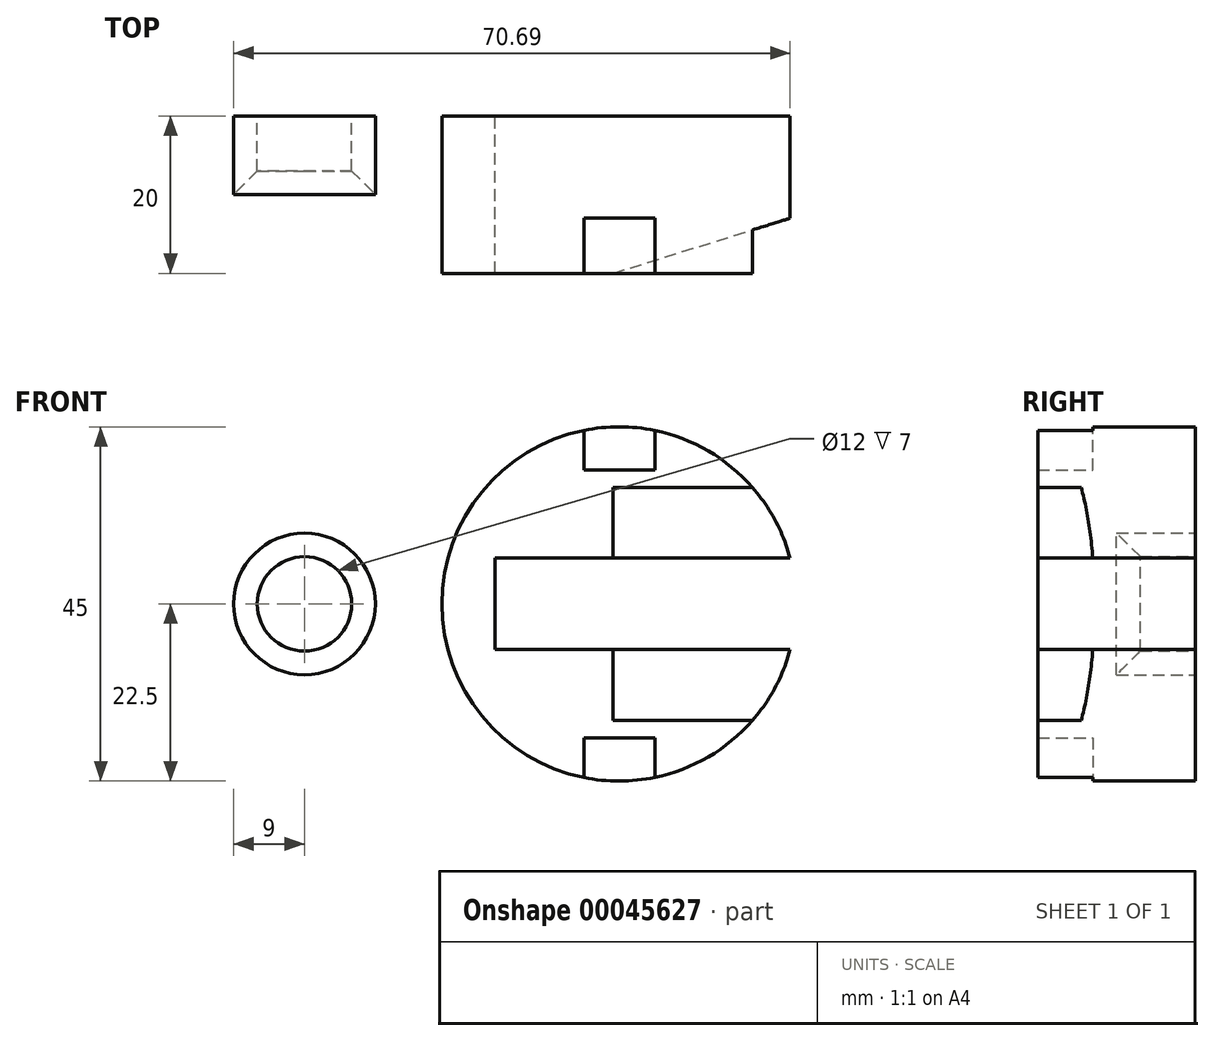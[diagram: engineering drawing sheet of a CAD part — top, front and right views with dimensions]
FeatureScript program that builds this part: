
annotation { "Feature Type Name" : "Feature", "Feature Type Description" : "" }
export const myFeature = defineFeature(function(context is Context, id is Id, definition is map)
    precondition{}
    {
        {
            var Q0;
            Q0=qCreatedBy(makeId("Front.planeOp"),FACE);
            var sketch = newSketch(context, id + "F0", { "sketchPlane" : qUnion([Q0])});
            skArc(sketch, "E0", {"start": v(-24.5, 0) * mm, "mid": v(-20.99, -8.49) * mm, "end": v(-12.5, -12) * mm});
            skLineSegment(sketch, "E1", {"start": v(-24.5, 0) * mm, "end": v(79.5, 0) * mm, "construction": true});
            skArc(sketch, "E2", {"start": v(-18.5, 0) * mm, "mid": v(-12.5, -6) * mm, "end": v(-6.5, 0) * mm});
            skArc(sketch, "E3", {"start": v(-21.5, 0) * mm, "mid": v(-12.5, -9) * mm, "end": v(-3.5, 0) * mm});
            skArc(sketch, "E4", {"start": v(4.95, 0) * mm, "mid": v(24.52, -22.3) * mm, "end": v(49.19, -5.8) * mm});
            skLineSegment(sketch, "E5", {"start": v(-12.5, -12) * mm, "end": v(6.27, -12) * mm});
            skArc(sketch, "E6", {"start": v(6.27, -12) * mm, "mid": v(7.65, -12.2) * mm, "end": v(8.92, -12.76) * mm});
            skLineSegment(sketch, "E7", {"start": v(11.69, -5.8) * mm, "end": v(49.19, -5.8) * mm});
            skLineSegment(sketch, "E8", {"start": v(11.69, -5.8) * mm, "end": v(11.69, 0) * mm});
            skLineSegment(sketch, "E9", {"start": v(27.5, -17) * mm, "end": v(32, -17) * mm});
            skLineSegment(sketch, "E10", {"start": v(23, -17) * mm, "end": v(23, -22.06) * mm});
            skLineSegment(sketch, "E11", {"start": v(32, -17) * mm, "end": v(32, -22.04) * mm});
            skLineSegment(sketch, "E12", {"start": v(27.5, -17) * mm, "end": v(23, -17) * mm});
            skArc(sketch, "E13.MirrorCS", {"start": v(-18.5, 0) * mm, "mid": v(-12.5, 6) * mm, "end": v(-6.5, 0) * mm});
            skArc(sketch, "E14.MirrorCS", {"start": v(-21.5, 0) * mm, "mid": v(-12.5, 9) * mm, "end": v(-3.5, 0) * mm});
            skArc(sketch, "E15.MirrorCS", {"start": v(-24.5, 0) * mm, "mid": v(-20.99, 8.49) * mm, "end": v(-12.5, 12) * mm});
            skLineSegment(sketch, "E16.MirrorCS", {"start": v(-12.5, 12) * mm, "end": v(6.27, 12) * mm});
            skArc(sketch, "E17.MirrorCS", {"start": v(6.27, 12) * mm, "mid": v(7.65, 12.2) * mm, "end": v(8.92, 12.76) * mm});
            skLineSegment(sketch, "E18.MirrorCS", {"start": v(27.5, 17) * mm, "end": v(32, 17) * mm});
            skLineSegment(sketch, "E19.MirrorCS", {"start": v(32, 17) * mm, "end": v(32, 22.04) * mm});
            skLineSegment(sketch, "E20.MirrorCS", {"start": v(27.5, 17) * mm, "end": v(23, 17) * mm});
            skLineSegment(sketch, "E21.MirrorCS", {"start": v(11.69, 5.8) * mm, "end": v(11.69, 0) * mm});
            skLineSegment(sketch, "E22.MirrorCS", {"start": v(11.69, 5.8) * mm, "end": v(49.19, 5.8) * mm});
            skArc(sketch, "E23.MirrorCS", {"start": v(4.95, 0) * mm, "mid": v(24.52, 22.3) * mm, "end": v(49.19, 5.8) * mm});
            skLineSegment(sketch, "E24.MirrorCS", {"start": v(23, 17) * mm, "end": v(23, 22.06) * mm});
            skLineSegment(sketch, "E25", {"start": v(27.45, -5.8) * mm, "end": v(27.45, -13.95) * mm});
            skLineSegment(sketch, "E26", {"start": v(27.45, -13.95) * mm, "end": v(45.1, -13.95) * mm});
            skLineSegment(sketch, "E27.MirrorCS", {"start": v(27.45, 13.95) * mm, "end": v(45.1, 13.95) * mm});
            skPoint(sketch, "E28", {"position": v(27.45, -5.8) * mm});
            skPoint(sketch, "E29", {"position": v(27.55, 5.8) * mm});
            skPoint(sketch, "E30.orphan", {"position": v(27.45, 13.95) * mm});
            skLineSegment(sketch, "E31", {"start": v(27.55, 5.8) * mm, "end": v(27.45, 13.95) * mm});
            skSolve(sketch);
        }
        {
            var Q0;
            {var subQ4=sQuery(id+"F0.wireOp",EDGE,"E6");Q0=makeQuery(id+"F0.imprint","IMPRINT",FACE,{"disambiguationData":[TD([[makeQuery(id+"F0.imprint","IMPRINT",EDGE,{"derivedFrom":subQ4}),1.0]])]});}
            var Q1;
            Q1=makeQuery(id+"F0.imprint","IMPRINT",FACE,{"disambiguationData":[TD([[makeQuery(id+"F0.imprint","IMPRINT",EDGE,{"derivedFrom":sQuery(id+"F0.wireOp",EDGE,"E2")}),-1.0]])]});
            extrude(context, id + "F1", {"entities" : qUnion([Q0, Q1]), "depth" : 10 * mm});
        }
        {
            var Q0;
            Q0=makeQuery(id+"F1.opExtrude","CAP_EDGE",EDGE,{"disambiguationData":[OSD([sQuery(id+"F0.wireOp",EDGE,"E2"),sQuery(id+"F0.wireOp",EDGE,"E13.MirrorCS")])],"isStart":false});
            chamfer(context, id + "F2", {"entities" : qUnion([Q0]), "chamferType" : ChamferType.OFFSET_ANGLE, "width" : 3 * mm, "oppositeDirection" : false, "angle" : 45 * degree, "tangentPropagation" : true});
        }
        {
            var Q0;
            {var subQ11=sQuery(id+"F0.wireOp",EDGE,"E8");Q0=makeQuery(id+"F0.imprint","IMPRINT",FACE,{"disambiguationData":[TD([[makeQuery(id+"F0.imprint","IMPRINT",EDGE,{"derivedFrom":subQ11}),1.0]])]});}
            var Q1;
            {var subQ0=sQuery(id+"F0.wireOp",EDGE,"E27.MirrorCS");Q1=makeQuery(id+"F0.imprint","IMPRINT",FACE,{"disambiguationData":[TD([[makeQuery(id+"F0.imprint","IMPRINT",EDGE,{"derivedFrom":subQ0}),-1.0]])]});}
            var Q2;
            {var subQ0=sQuery(id+"F0.wireOp",EDGE,"E26");Q2=makeQuery(id+"F0.imprint","IMPRINT",FACE,{"disambiguationData":[TD([[makeQuery(id+"F0.imprint","IMPRINT",EDGE,{"derivedFrom":subQ0}),1.0]])]});}
            extrude(context, id + "F3", {"entities" : qUnion([Q0, Q1, Q2]), "operationType" : NewBodyOperationType.ADD, "depth" : 20 * mm});
        }
        {
            var Q0;
            Q0=makeQuery(id+"F0.imprint","IMPRINT",FACE,{"disambiguationData":[TD([[makeQuery(id+"F0.imprint","IMPRINT",EDGE,{"derivedFrom":sQuery(id+"F0.wireOp",EDGE,"E18.MirrorCS")}),1.0]])]});
            var Q1;
            Q1=makeQuery(id+"F0.imprint","IMPRINT",FACE,{"disambiguationData":[TD([[makeQuery(id+"F0.imprint","IMPRINT",EDGE,{"derivedFrom":sQuery(id+"F0.wireOp",EDGE,"E9")}),-1.0]])]});
            extrude(context, id + "F4", {"entities" : qUnion([Q0, Q1]), "operationType" : NewBodyOperationType.ADD, "depth" : 13 * mm});
        }
        {
            var Q0;
            Q0=makeQuery(id+"F3.opExtrude","SWEPT_FACE",FACE,{"disambiguationData":[OSD([sQuery(id+"F0.wireOp",EDGE,"E22.MirrorCS")])]});
            var sketch = newSketch(context, id + "F5", { "sketchPlane" : qUnion([Q0])});
            skLineSegment(sketch, "E32", {"start": v(49.19, 20) * mm, "end": v(26.69, 20) * mm});
            skLineSegment(sketch, "E33", {"start": v(26.69, 20) * mm, "end": v(49.19, 13) * mm});
            skSolve(sketch);
        }
        {
            var Q0;
            Q0 = qSketchRegion(id + "F5", true);
            var Q1;
            {var subQ0=sQuery(id+"F5.wireOp",EDGE,"E32");Q1=makeQuery(id+"F5.imprint","IMPRINT",FACE,{"disambiguationData":[TD([[makeQuery(id+"F5.imprint","IMPRINT",EDGE,{"derivedFrom":subQ0}),-1.0]])]});}
            extrude(context, id + "F6", {"entities" : qUnion([Q0, Q1]), "operationType" : NewBodyOperationType.REMOVE, "oppositeDirection" : true, "depth" : 9 * mm});
        }
        {
            var Q0;
            Q0=makeQuery(id+"F3.opExtrude","SWEPT_FACE",FACE,{"disambiguationData":[OSD([sQuery(id+"F0.wireOp",EDGE,"E7")])]});
            var sketch = newSketch(context, id + "F7", { "sketchPlane" : qUnion([Q0])});
            skLineSegment(sketch, "E34", {"start": v(49.19, -20) * mm, "end": v(26.69, -20) * mm});
            skLineSegment(sketch, "E35", {"start": v(26.69, -20) * mm, "end": v(49.19, -13) * mm});
            skSolve(sketch);
        }
        {
            var Q0;
            {var subQ0=sQuery(id+"F7.wireOp",EDGE,"E34");Q0=makeQuery(id+"F7.imprint","IMPRINT",FACE,{"disambiguationData":[TD([[makeQuery(id+"F7.imprint","IMPRINT",EDGE,{"derivedFrom":subQ0}),1.0]])]});}
            extrude(context, id + "F8", {"entities" : qUnion([Q0]), "operationType" : NewBodyOperationType.REMOVE, "oppositeDirection" : true, "depth" : 9 * mm});
        }
    });
